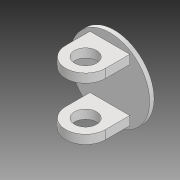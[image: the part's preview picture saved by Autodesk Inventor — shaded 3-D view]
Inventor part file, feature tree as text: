
AUTODESK INVENTOR PART (.ipt)
format: ipt  version: 2020 (Build 240168000, 168)  size: 114,176 bytes
history: native  units: mm
features: extrude x2, sketch x2, plane x1, mirror x1
ambient origin geometry x8: Origin, YZ Plane, XZ Plane, XY Plane, X Axis, Y Axis, Z Axis, Center Point
bodies: Solid1 (feature_tree)
feature tree (6):
  extrude  "Extrusion1"  Depth=10.0mm TaperAngle=0.0deg
  plane  "Work Plane1"
  extrude  "Extrusion2"  Depth=45.0mm
  mirror  "Mirror1"
  sketch  "Sketch1"  dims[d0=180.0mm d1=10.0mm d2=0.0mm]
  sketch  "Sketch2"  dims[d3=50.0mm d4=45.0mm d5=100.0mm d6=50.0mm d7=20.0mm d8=0.0mm]
